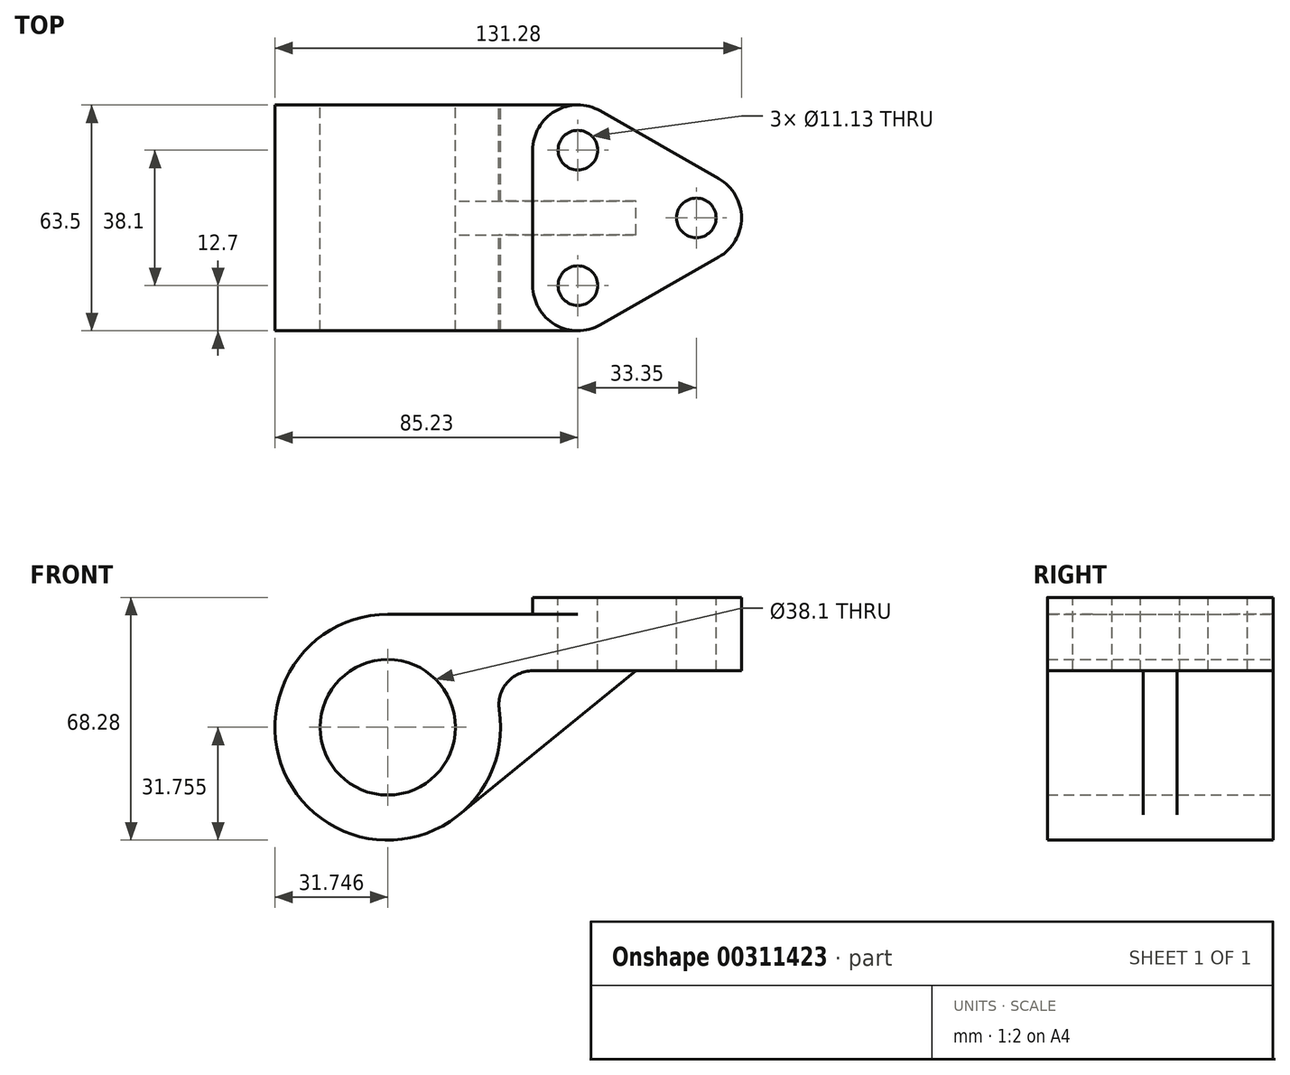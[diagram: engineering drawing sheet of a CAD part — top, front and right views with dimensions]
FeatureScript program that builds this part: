
annotation { "Feature Type Name" : "Feature", "Feature Type Description" : "" }
export const myFeature = defineFeature(function(context is Context, id is Id, definition is map)
    precondition{}
    {
        {
            var Q0;
            Q0=qCreatedBy(makeId("Top.planeOp"),FACE);
            var sketch = newSketch(context, id + "F0", { "sketchPlane" : qUnion([Q0])});
            skLineSegment(sketch, "E0", {"start": v(0, 19.05) * mm, "end": v(0, -19.05) * mm});
            skArc(sketch, "E1", {"start": v(0, -19.05) * mm, "mid": v(6.32, -30.03) * mm, "end": v(19, -30.08) * mm});
            skLineSegment(sketch, "E2", {"start": v(19, -30.08) * mm, "end": v(52.35, -11.03) * mm});
            skArc(sketch, "E3", {"start": v(52.35, -11.03) * mm, "mid": v(58.75, 0) * mm, "end": v(52.35, 11.03) * mm});
            skLineSegment(sketch, "E4", {"start": v(52.35, 11.03) * mm, "end": v(19, 30.08) * mm});
            skArc(sketch, "E5", {"start": v(19, 30.08) * mm, "mid": v(6.32, 30.03) * mm, "end": v(0, 19.05) * mm});
            skCircle(sketch, "E6", {"center": v(12.7, 19.05) * mm, "radius": 5.56 * mm});
            skCircle(sketch, "E7", {"center": v(46.05, 0) * mm, "radius": 5.56 * mm});
            skCircle(sketch, "E8", {"center": v(12.7, -19.05) * mm, "radius": 5.56 * mm});
            skSolve(sketch);
        }
        {
            var Q0;
            Q0 = qSketchRegion(id + "F0", true);
            extrude(context, id + "F1", {"entities" : qUnion([Q0]), "oppositeDirection" : true, "depth" : 20.65 * mm});
        }
        {
            var Q0;
            Q0=qCreatedBy(makeId("Front.planeOp"),FACE);
            var sketch = newSketch(context, id + "F2", { "sketchPlane" : qUnion([Q0])});
            skCircle(sketch, "E9", {"center": v(-40.78, -36.53) * mm, "radius": 19.05 * mm});
            skArc(sketch, "E10", {"start": v(-40.78, -4.78) * mm, "mid": v(-61.44, -60.64) * mm, "end": v(-9.41, -31.64) * mm});
            skLineSegment(sketch, "E11", {"start": v(-40.78, -4.78) * mm, "end": v(12.7, -4.78) * mm});
            skArc(sketch, "E12", {"start": v(0, -20.65) * mm, "mid": v(-7.23, -23.98) * mm, "end": v(-9.41, -31.64) * mm});
            skLineSegment(sketch, "E13", {"start": v(0, -20.65) * mm, "end": v(12.7, -20.65) * mm});
            skLineSegment(sketch, "E14", {"start": v(12.7, -4.78) * mm, "end": v(12.7, -20.65) * mm});
            skSolve(sketch);
        }
        {
            var Q0;
            Q0 = qSketchRegion(id + "F2", true);
            extrude(context, id + "F3", {"entities" : qUnion([Q0]), "operationType" : NewBodyOperationType.ADD, "endBound" : BoundingType.SYMMETRIC, "depth" : 63.5 * mm});
        }
        {
            var Q0;
            Q0=qCreatedBy(makeId("Front.planeOp"),FACE);
            var sketch = newSketch(context, id + "F4", { "sketchPlane" : qUnion([Q0])});
            skLineSegment(sketch, "E15", {"start": v(-20.75, -61.16) * mm, "end": v(29.07, -20.65) * mm});
            skCircle(sketch, "E16", {"center": v(-40.78, -36.53) * mm, "radius": 19.05 * mm, "construction": true});
            skLineSegment(sketch, "E17", {"start": v(29.07, -20.65) * mm, "end": v(0, -20.65) * mm});
            skArc(sketch, "E18", {"start": v(0, -20.65) * mm, "mid": v(-7.23, -23.98) * mm, "end": v(-9.41, -31.64) * mm});
            skArc(sketch, "E19", {"start": v(-20.75, -61.16) * mm, "mid": v(-11.15, -47.91) * mm, "end": v(-9.41, -31.64) * mm});
            skSolve(sketch);
        }
        {
            var Q0;
            Q0 = qSketchRegion(id + "F4", true);
            extrude(context, id + "F5", {"entities" : qUnion([Q0]), "operationType" : NewBodyOperationType.ADD, "endBound" : BoundingType.SYMMETRIC, "depth" : 9.52 * mm});
        }
        {
            var Q0;
            Q0=makeQuery(id+"F1.opExtrude","CAP_FACE",FACE,{"disambiguationData":[OSD([sQuery(id+"F0.wireOp",EDGE,"E0"),sQuery(id+"F0.wireOp",EDGE,"E1"),sQuery(id+"F0.wireOp",EDGE,"E2"),sQuery(id+"F0.wireOp",EDGE,"E3"),sQuery(id+"F0.wireOp",EDGE,"E4"),sQuery(id+"F0.wireOp",EDGE,"E5"),sQuery(id+"F0.wireOp",EDGE,"E6"),sQuery(id+"F0.wireOp",EDGE,"E7"),sQuery(id+"F0.wireOp",EDGE,"E8")])],"isStart":true});
            var sketch = newSketch(context, id + "F6", { "sketchPlane" : qUnion([Q0])});
            skCircle(sketch, "E20", {"center": v(12.7, -19.05) * mm, "radius": 5.56 * mm});
            skCircle(sketch, "E21", {"center": v(12.7, 19.05) * mm, "radius": 5.56 * mm});
            skSolve(sketch);
        }
        {
            var Q0;
            Q0 = qSketchRegion(id + "F6", true);
            extrude(context, id + "F7", {"entities" : qUnion([Q0]), "operationType" : NewBodyOperationType.REMOVE, "endBound" : BoundingType.THROUGH_ALL, "oppositeDirection" : true, "depth" : 25.4 * mm});
        }
    });
